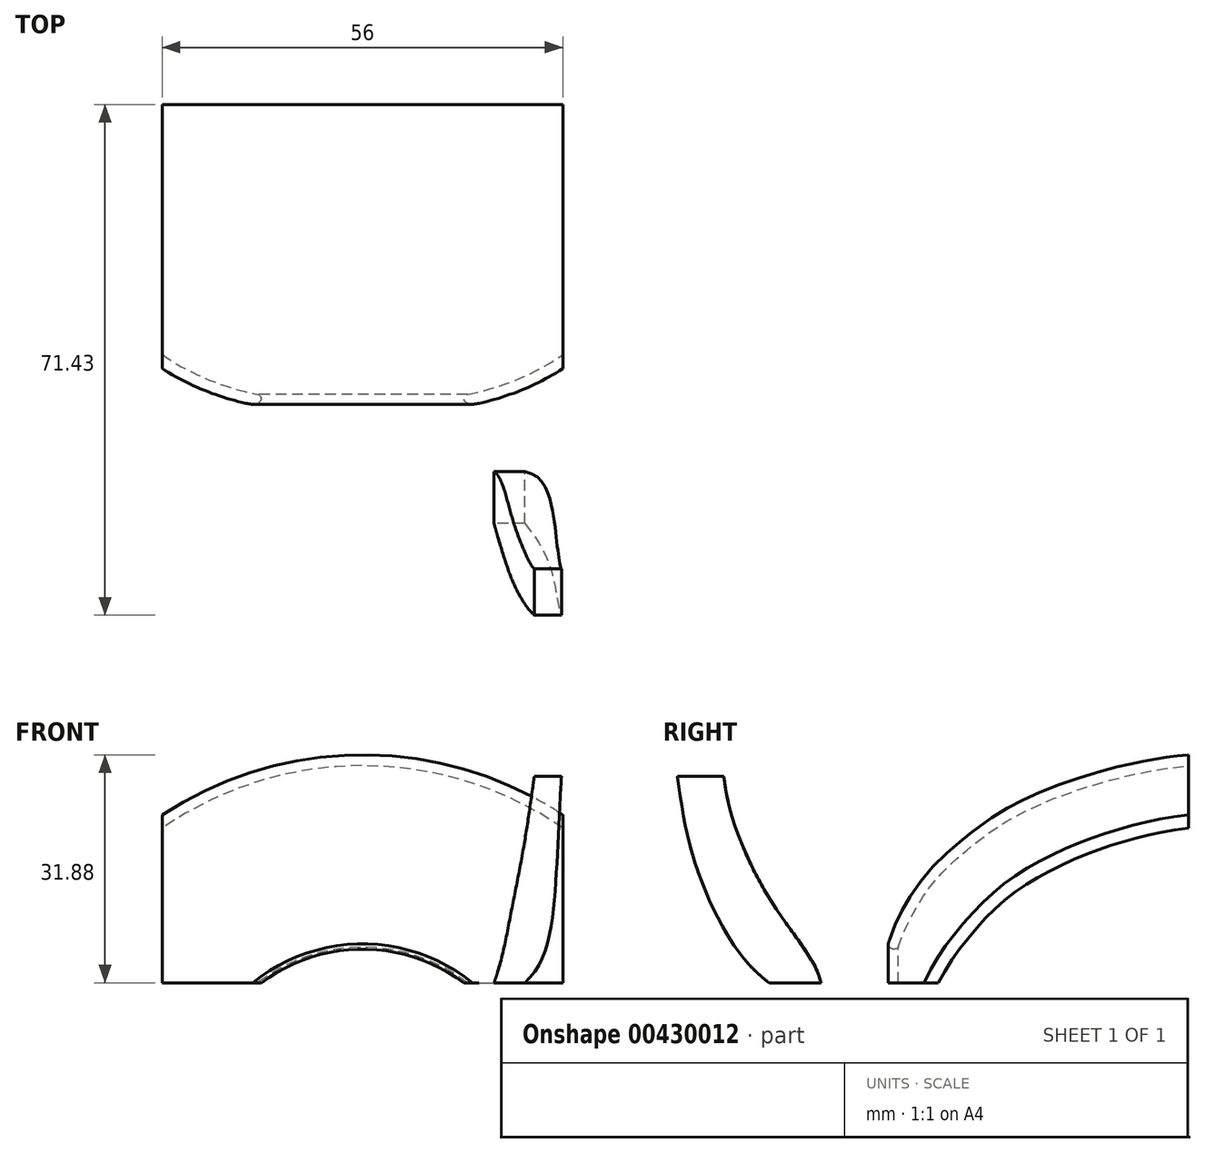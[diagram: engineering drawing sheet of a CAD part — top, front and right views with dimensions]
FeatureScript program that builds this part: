
annotation { "Feature Type Name" : "Feature", "Feature Type Description" : "" }
export const myFeature = defineFeature(function(context is Context, id is Id, definition is map)
    precondition{}
    {
        {
            var Q0;
            Q0=qCreatedBy(makeId("Front.planeOp"),FACE);
            var sketch = newSketch(context, id + "F0", { "sketchPlane" : qUnion([Q0])});
            skLineSegment(sketch, "E0", {"start": v(-27.8, 28.47) * mm, "end": v(27.8, 28.47) * mm, "construction": true});
            skLineSegment(sketch, "E1", {"start": v(-27.3, 19.07) * mm, "end": v(27.3, 19.07) * mm, "construction": true});
            skLineSegment(sketch, "E2", {"start": v(-26.65, 9.67) * mm, "end": v(26.65, 9.67) * mm, "construction": true});
            skPoint(sketch, "E2.startSnap0", {"position": v(0, 9.67) * mm});
            skLineSegment(sketch, "E3", {"start": v(-24.05, 1.17) * mm, "end": v(24.05, 1.17) * mm, "construction": true});
            skLineSegment(sketch, "E4", {"start": v(-16.7, -4.33) * mm, "end": v(16.7, -4.33) * mm, "construction": true});
            skFitSpline(sketch, "E5", {"points": [v(27.8, 28.47) * mm, v(27.3, 19.07) * mm, v(26.65, 9.67) * mm, v(24.05, 1.17) * mm, v(16.7, -4.33) * mm], "startDerivative": vector(-2.06, -37.27) * mm, "endDerivative": vector(-34, -18.84) * mm});
            skLineSegment(sketch, "E6", {"start": v(0, 28.47) * mm, "end": v(0, -4.33) * mm});
            skLineSegment(sketch, "E7", {"start": v(0, 28.47) * mm, "end": v(24, 28.47) * mm});
            skLineSegment(sketch, "E8", {"start": v(0, 19.07) * mm, "end": v(22.6, 19.07) * mm});
            skLineSegment(sketch, "E9", {"start": v(0, 9.67) * mm, "end": v(20.8, 9.67) * mm});
            skLineSegment(sketch, "E10", {"start": v(0, 1.17) * mm, "end": v(18.9, 1.17) * mm});
            skFitSpline(sketch, "E11", {"points": [v(24, 28.47) * mm, v(22.6, 19.07) * mm, v(20.8, 9.67) * mm, v(18.9, 1.17) * mm, v(16.7, -4.33) * mm], "startDerivative": vector(-4.85, -35.3) * mm, "endDerivative": vector(-11.16, -24.5) * mm});
            skLineSegment(sketch, "E12", {"start": v(24, 28.47) * mm, "end": v(27.8, 28.47) * mm});
            skSolve(sketch);
        }
        {
            var Q0;
            {var subQ5=sQuery(id+"F0.wireOp",EDGE,"E5");Q0=makeQuery(id+"F0.imprint","IMPRINT",FACE,{"disambiguationData":[TD([[makeQuery(id+"F0.imprint","IMPRINT",EDGE,{"derivedFrom":subQ5}),-1.0]])]});}
            extrude(context, id + "F1", {"entities" : qUnion([Q0]), "depth" : 29 * mm});
        }
        {
            var Q0;
            Q0=qCreatedBy(makeId("Right.planeOp"),FACE);
            var sketch = newSketch(context, id + "F2", { "sketchPlane" : qUnion([Q0])});
            skLineSegment(sketch, "E13.0", {"start": v(-29, 28.47) * mm, "end": v(0, 28.47) * mm});
            skFitSpline(sketch, "E14.0", {"points": [v(0, 28.47) * mm, v(0, 25.33) * mm, v(0, 19.05) * mm, v(0, 9.83) * mm, v(0, 1.2) * mm, v(0, -2.61) * mm, v(0, -4.33) * mm]});
            skPoint(sketch, "E15", {"position": v(0, 19.07) * mm});
            skPoint(sketch, "E16", {"position": v(0, 9.67) * mm});
            skPoint(sketch, "E17", {"position": v(0, 1.17) * mm});
            skLineSegment(sketch, "E18", {"start": v(0, 19.07) * mm, "end": v(-27.3, 19.07) * mm, "construction": true});
            skLineSegment(sketch, "E19", {"start": v(0, 9.67) * mm, "end": v(-23.8, 9.67) * mm, "construction": true});
            skLineSegment(sketch, "E20", {"start": v(0, 1.17) * mm, "end": v(-18, 1.17) * mm, "construction": true});
            skLineSegment(sketch, "E21", {"start": v(0, -4.33) * mm, "end": v(-9.5, -4.33) * mm});
            skFitSpline(sketch, "E22", {"points": [v(-29, 28.47) * mm, v(-27.3, 19.07) * mm, v(-23.8, 9.67) * mm, v(-18, 1.17) * mm, v(-9.5, -4.33) * mm], "startDerivative": vector(5.53, -38.63) * mm, "endDerivative": vector(36.2, -19.02) * mm});
            skSolve(sketch);
        }
        {
            var Q0;
            Q0=makeQuery(id+"F2.imprint","IMPRINT",FACE,{"disambiguationData":[TD([[makeQuery(id+"F2.imprint","IMPRINT",EDGE,{"derivedFrom":sQuery(id+"F2.wireOp",EDGE,"E13.0")}),-1.0]])]});
            extrude(context, id + "F3", {"entities" : qUnion([Q0]), "operationType" : NewBodyOperationType.INTERSECT, "depth" : 30 * mm});
        }
        {
            var Q0;
            Q0=qCreatedBy(makeId("Right.planeOp"),FACE);
            var sketch = newSketch(context, id + "F4", { "sketchPlane" : qUnion([Q0])});
            skPoint(sketch, "E23", {"position": v(0, 19.07) * mm});
            skPoint(sketch, "E24", {"position": v(0, 9.67) * mm});
            skPoint(sketch, "E25", {"position": v(0, 1.17) * mm});
            skLineSegment(sketch, "E26", {"start": v(0, 19.07) * mm, "end": v(-20, 19.07) * mm, "construction": true});
            skLineSegment(sketch, "E27", {"start": v(0, 9.67) * mm, "end": v(-15, 9.67) * mm, "construction": true});
            skLineSegment(sketch, "E28", {"start": v(0, 0) * mm, "end": v(-9, 0) * mm, "construction": true});
            skFitSpline(sketch, "E29", {"points": [v(-22.5, 28.47) * mm, v(-20, 19.07) * mm, v(-15, 9.67) * mm, v(-9, 0) * mm, v(-9.55, -4.35) * mm], "startDerivative": vector(5.9, -45.27) * mm, "endDerivative": vector(-8.24, -22.63) * mm});
            skFitSpline(sketch, "E30.0", {"points": [v(-9.5, -4.33) * mm, v(-10.96, -3.56) * mm, v(-13.16, -2.4) * mm, v(-15.9, -0.62) * mm, v(-17.5, 0.66) * mm, v(-18.67, 1.82) * mm, v(-19.51, 2.76) * mm, v(-20.3, 3.76) * mm, v(-21.04, 4.8) * mm, v(-21.72, 5.85) * mm, v(-22.58, 7.3) * mm, v(-23.57, 9.15) * mm, v(-24.64, 11.43) * mm, v(-25.61, 13.78) * mm, v(-26.46, 16.14) * mm, v(-27.19, 18.55) * mm, v(-27.77, 20.99) * mm, v(-28.4, 24.3) * mm, v(-28.76, 26.8) * mm, v(-29, 28.47) * mm]});
            skLineSegment(sketch, "E31", {"start": v(-22.5, 28.47) * mm, "end": v(-29, 28.47) * mm});
            skLineSegment(sketch, "E32", {"start": v(0, -4.33) * mm, "end": v(-9.5, -4.33) * mm});
            skLineSegment(sketch, "E33", {"start": v(0, 19.07) * mm, "end": v(0, 0) * mm, "construction": true});
            skSolve(sketch);
        }
        {
            var Q0;
            {var subQ0=sQuery(id+"F4.wireOp",EDGE,"E31");Q0=makeQuery(id+"F4.imprint","IMPRINT",FACE,{"disambiguationData":[TD([[makeQuery(id+"F4.imprint","IMPRINT",EDGE,{"derivedFrom":subQ0}),1.0]])]});}
            extrude(context, id + "F5", {"entities" : qUnion([Q0]), "operationType" : NewBodyOperationType.INTERSECT, "depth" : 50 * mm});
        }
        {
            var Q0;
            Q0=makeQuery(id+"F1.opExtrude","SWEPT_FACE",FACE,{"disambiguationData":[OSD([sQuery(id+"F0.wireOp",EDGE,"E12")])]});
            cPlane(context, id + "F6", {"entities" : qUnion([Q0]), "cplaneType" : CPlaneType.OFFSET, "offset" : 0 * mm, "width" : 150 * mm, "height" : 150 * mm});
        }
        {
            var Q0;
            Q0=qCreatedBy(id+"F6.planeOp",FACE);
            cPlane(context, id + "F7", {"entities" : qUnion([Q0]), "cplaneType" : CPlaneType.OFFSET, "offset" : 32.8 * mm, "oppositeDirection" : true, "width" : 150 * mm, "height" : 150 * mm});
        }
        {
            var Q0;
            Q0=qCreatedBy(makeId("Right.planeOp"),FACE);
            var sketch = newSketch(context, id + "F8", { "sketchPlane" : qUnion([Q0])});
            skLineSegment(sketch, "E34", {"start": v(42.71, 30.03) * mm, "end": v(42.71, -7.37) * mm, "construction": true});
            skLineSegment(sketch, "E35", {"start": v(32.11, -7.37) * mm, "end": v(32.11, 28.13) * mm, "construction": true});
            skLineSegment(sketch, "E36", {"start": v(23.71, -7.37) * mm, "end": v(23.71, 25.43) * mm, "construction": true});
            skLineSegment(sketch, "E37", {"start": v(16.71, -7.37) * mm, "end": v(16.71, 22.03) * mm, "construction": true});
            skLineSegment(sketch, "E38", {"start": v(11.11, -7.37) * mm, "end": v(11.11, 17.88) * mm, "construction": true});
            skLineSegment(sketch, "E39", {"start": v(6.01, -7.37) * mm, "end": v(6.01, 12.63) * mm, "construction": true});
            skLineSegment(sketch, "E40", {"start": v(1.91, -7.37) * mm, "end": v(1.91, 4.63) * mm, "construction": true});
            skLineSegment(sketch, "E41", {"start": v(1.91, -7.37) * mm, "end": v(1.91, 2.33) * mm, "construction": true});
            skLineSegment(sketch, "E42", {"start": v(1.91, 2.33) * mm, "end": v(6.01, 2.63) * mm});
            skLineSegment(sketch, "E43", {"start": v(6.01, 2.63) * mm, "end": v(11.11, 2.63) * mm});
            skLineSegment(sketch, "E44", {"start": v(11.11, 2.63) * mm, "end": v(16.71, 2.63) * mm});
            skLineSegment(sketch, "E45", {"start": v(16.71, 2.63) * mm, "end": v(23.71, 2.63) * mm});
            skLineSegment(sketch, "E46", {"start": v(23.71, 2.63) * mm, "end": v(32.11, 2.63) * mm});
            skLineSegment(sketch, "E47", {"start": v(32.11, 2.63) * mm, "end": v(42.71, 2.63) * mm});
            skFitSpline(sketch, "E48", {"points": [v(1.91, 4.63) * mm, v(6.01, 12.63) * mm, v(11.11, 17.88) * mm, v(16.71, 22.03) * mm, v(23.71, 25.43) * mm, v(32.11, 28.13) * mm, v(42.71, 30.03) * mm], "startDerivative": vector(12.07, 40.08) * mm, "endDerivative": vector(65.72, 7.02) * mm});
            skFitSpline(sketch, "E49.0", {"points": [v(0.47, 5.06) * mm, v(0.61, 5.52) * mm, v(0.95, 6.49) * mm, v(1.83, 8.56) * mm, v(2.97, 10.73) * mm, v(4.26, 12.78) * mm, v(5.29, 14.2) * mm, v(6.34, 15.45) * mm, v(7.42, 16.58) * mm, v(8.5, 17.61) * mm, v(9.6, 18.57) * mm, v(10.7, 19.49) * mm, v(11.82, 20.4) * mm, v(12.98, 21.3) * mm, v(14.2, 22.18) * mm, v(15.45, 23.02) * mm, v(17.2, 24.08) * mm, v(19.5, 25.28) * mm, v(22.4, 26.55) * mm, v(25.44, 27.7) * mm, v(28.58, 28.72) * mm, v(31.8, 29.62) * mm, v(35.06, 30.39) * mm, v(38.56, 31.03) * mm, v(41.16, 31.37) * mm, v(42.55, 31.52) * mm]});
            skLineSegment(sketch, "E50", {"start": v(42.39, 31.5) * mm, "end": v(42.71, 30.03) * mm, "construction": true});
            skLineSegment(sketch, "E51", {"start": v(0.67, 5.66) * mm, "end": v(1.91, 4.63) * mm, "construction": true});
            skArc(sketch, "E52", {"start": v(0.67, 5.66) * mm, "mid": v(0.77, 4.52) * mm, "end": v(1.91, 4.63) * mm});
            skArc(sketch, "E53", {"start": v(42.71, 30.03) * mm, "mid": v(43.29, 30.93) * mm, "end": v(42.39, 31.5) * mm});
            skLineSegment(sketch, "E54", {"start": v(-56.5, -52.67) * mm, "end": v(-23, -52.67) * mm});
            skLineSegment(sketch, "E55", {"start": v(-39.76, -52.67) * mm, "end": v(-39.76, -49.97) * mm});
            skArc(sketch, "E56", {"start": v(-23, -52.67) * mm, "mid": v(-39.76, -49.97) * mm, "end": v(-56.5, -52.67) * mm});
            skLineSegment(sketch, "E57", {"start": v(1.91, 4.63) * mm, "end": v(1.91, -19.37) * mm, "construction": true});
            skLineSegment(sketch, "E58", {"start": v(1.91, -19.37) * mm, "end": v(46.6, -19.37) * mm});
            skSolve(sketch);
        }
        {
            var Q0;
            Q0=makeQuery(id+"F8.imprint","IMPRINT",FACE,{"disambiguationData":[TD([[makeQuery(id+"F8.imprint","IMPRINT",EDGE,{"derivedFrom":sQuery(id+"F8.wireOp",EDGE,"E48")}),1.0]])]});
            var Q1;
            Q1=sQuery(id+"F8.wireOp",EDGE,"E58");
            revolve(context, id + "F9", {"entities" : qUnion([Q0]), "axis" : qUnion([Q1]), "revolveType" : RevolveType.FULL});
        }
        {
            var Q0;
            Q0=qCreatedBy(makeId("Right.planeOp"),FACE);
            var sketch = newSketch(context, id + "F10", { "sketchPlane" : qUnion([Q0])});
            skLineSegment(sketch, "E59", {"start": v(-1.05, -0.37) * mm, "end": v(-1.05, -142.76) * mm});
            skLineSegment(sketch, "E60", {"start": v(-1.05, -142.76) * mm, "end": v(51.64, -142.76) * mm});
            skLineSegment(sketch, "E61", {"start": v(51.64, -142.76) * mm, "end": v(51.64, 39.81) * mm});
            skLineSegment(sketch, "E62", {"start": v(51.64, 39.81) * mm, "end": v(42.43, 31.88) * mm});
            skLineSegment(sketch, "E63", {"start": v(42.43, 31.88) * mm, "end": v(42.43, -0.37) * mm});
            skLineSegment(sketch, "E64", {"start": v(42.43, -0.37) * mm, "end": v(-1.05, -0.37) * mm});
            skSolve(sketch);
        }
        {
            var Q0;
            Q0=makeQuery(id+"F10.imprint","IMPRINT",FACE,{"disambiguationData":[TD([[makeQuery(id+"F10.imprint","IMPRINT",EDGE,{"derivedFrom":sQuery(id+"F10.wireOp",EDGE,"E59")}),1.0]])]});
            extrude(context, id + "F11", {"entities" : qUnion([Q0]), "operationType" : NewBodyOperationType.REMOVE, "depth" : 90 * mm, "hasSecondDirection" : true, "secondDirectionOppositeDirection" : true, "secondDirectionDepth" : 90 * mm});
        }
        {
            var Q0;
            Q0=makeQuery(id+"F11.boolean.opBoolean","COPY",FACE,{"disambiguationData":[OD(0.0)],"derivedFrom":makeQuery(id+"F11.opExtrude","SWEPT_FACE",FACE,{"disambiguationData":[OSD([sQuery(id+"F10.wireOp",EDGE,"E64")])]})});
            var sketch = newSketch(context, id + "F12", { "sketchPlane" : qUnion([Q0])});
            skLineSegment(sketch, "E65.bottom", {"start": v(-28, -50) * mm, "end": v(28, -50) * mm});
            skLineSegment(sketch, "E65.top", {"start": v(-28, 50) * mm, "end": v(28, 50) * mm});
            skLineSegment(sketch, "E65.left", {"start": v(-28, -50) * mm, "end": v(-28, 50) * mm});
            skLineSegment(sketch, "E65.right", {"start": v(28, -50) * mm, "end": v(28, 50) * mm});
            skPoint(sketch, "E65.middle", {"position": v(0, 0) * mm});
            skSolve(sketch);
        }
        {
            var Q0;
            {var subQ5=sQuery(id+"F12.wireOp",EDGE,"E65.bottom");Q0=makeQuery(id+"F12.imprint","IMPRINT",FACE,{"disambiguationData":[TD([[makeQuery(id+"F12.imprint","IMPRINT",EDGE,{"derivedFrom":subQ5}),1.0]])]});}
            var Q1;
            {var subQ1=makeQuery(id+"F11.opExtrude","SWEPT_FACE",FACE,{"disambiguationData":[OSD([sQuery(id+"F10.wireOp",EDGE,"E64")])]});var subQ6=makeQuery(id+"F11.boolean.opBoolean","INTERSECT",EDGE,{"disambiguationData":[OD(0.0)],"derivedFrom":[makeQuery(id+"F9.opRevolve","SWEPT_FACE",FACE,{"disambiguationData":[OSD([sQuery(id+"F8.wireOp",EDGE,"E52")])]}),subQ1]});Q1=makeQuery(id+"F12.imprint","IMPRINT",FACE,{"disambiguationData":[TD([[makeQuery(id+"F12.imprint","IMPRINT",EDGE,{"derivedFrom":subQ6}),1.0]])]});}
            extrude(context, id + "F13", {"entities" : qUnion([Q0, Q1]), "operationType" : NewBodyOperationType.INTERSECT, "oppositeDirection" : true, "depth" : 40 * mm});
        }
    });
